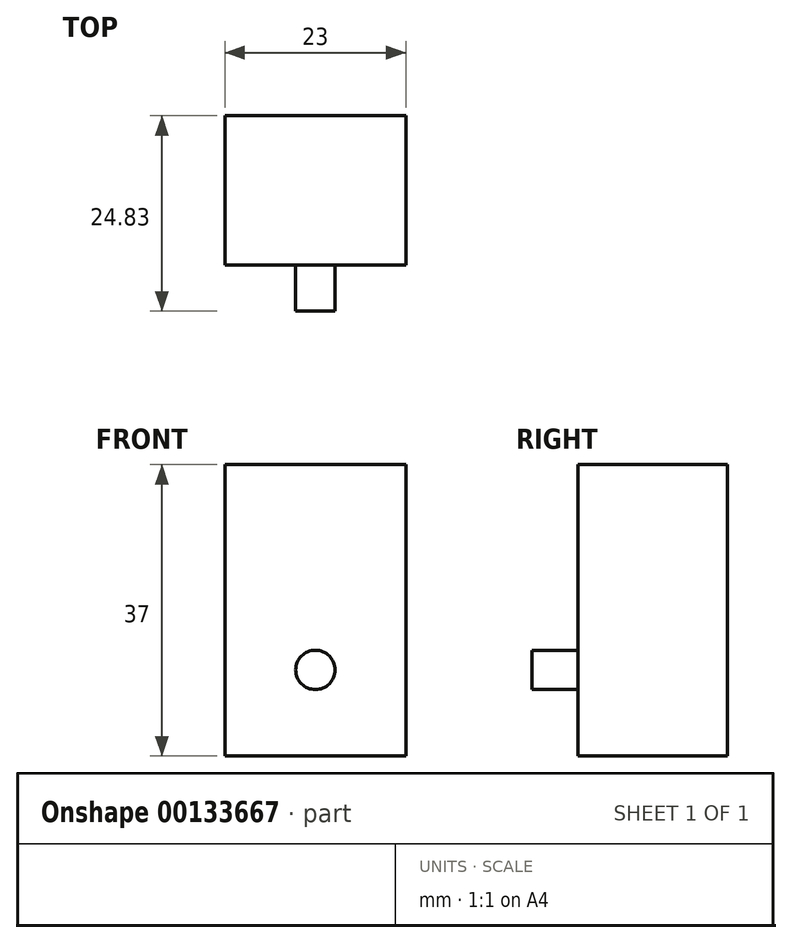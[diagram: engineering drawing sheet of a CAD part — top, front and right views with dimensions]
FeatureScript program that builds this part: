
annotation { "Feature Type Name" : "Feature", "Feature Type Description" : "" }
export const myFeature = defineFeature(function(context is Context, id is Id, definition is map)
    precondition{}
    {
        {
            var Q0;
            Q0=qCreatedBy(makeId("Top.planeOp"),FACE);
            var sketch = newSketch(context, id + "F0", { "sketchPlane" : qUnion([Q0])});
            skLineSegment(sketch, "E0.bottom", {"start": v(-11.5, 9.5) * mm, "end": v(11.5, 9.5) * mm});
            skLineSegment(sketch, "E0.top", {"start": v(-11.5, -9.5) * mm, "end": v(11.5, -9.5) * mm});
            skLineSegment(sketch, "E0.left", {"start": v(-11.5, 9.5) * mm, "end": v(-11.5, -9.5) * mm});
            skLineSegment(sketch, "E0.right", {"start": v(11.5, 9.5) * mm, "end": v(11.5, -9.5) * mm});
            skPoint(sketch, "E0.middle", {"position": v(0, 0) * mm});
            skSolve(sketch);
        }
        {
            var Q0;
            Q0=makeQuery(id+"F0.imprint","IMPRINT",FACE,{"disambiguationData":[TD([[makeQuery(id+"F0.imprint","IMPRINT",EDGE,{"derivedFrom":sQuery(id+"F0.wireOp",EDGE,"E0.bottom")}),-1.0]])]});
            extrude(context, id + "F1", {"entities" : qUnion([Q0]), "depth" : 37 * mm});
        }
        {
            var Q0;
            Q0=makeQuery(id+"F1.opExtrude","SWEPT_FACE",FACE,{"disambiguationData":[OSD([sQuery(id+"F0.wireOp",EDGE,"E0.top")])]});
            var sketch = newSketch(context, id + "F2", { "sketchPlane" : qUnion([Q0])});
            skCircle(sketch, "E1", {"center": v(0, 10.92) * mm, "radius": 2.5 * mm});
            skSolve(sketch);
        }
        {
            var Q0;
            Q0=makeQuery(id+"F2.imprint","IMPRINT",FACE,{"disambiguationData":[TD([[makeQuery(id+"F2.imprint","IMPRINT",EDGE,{"derivedFrom":sQuery(id+"F2.wireOp",EDGE,"E1")}),1.0]])]});
            extrude(context, id + "F3", {"entities" : qUnion([Q0]), "operationType" : NewBodyOperationType.ADD, "depth" : 5.83 * mm});
        }
    });
